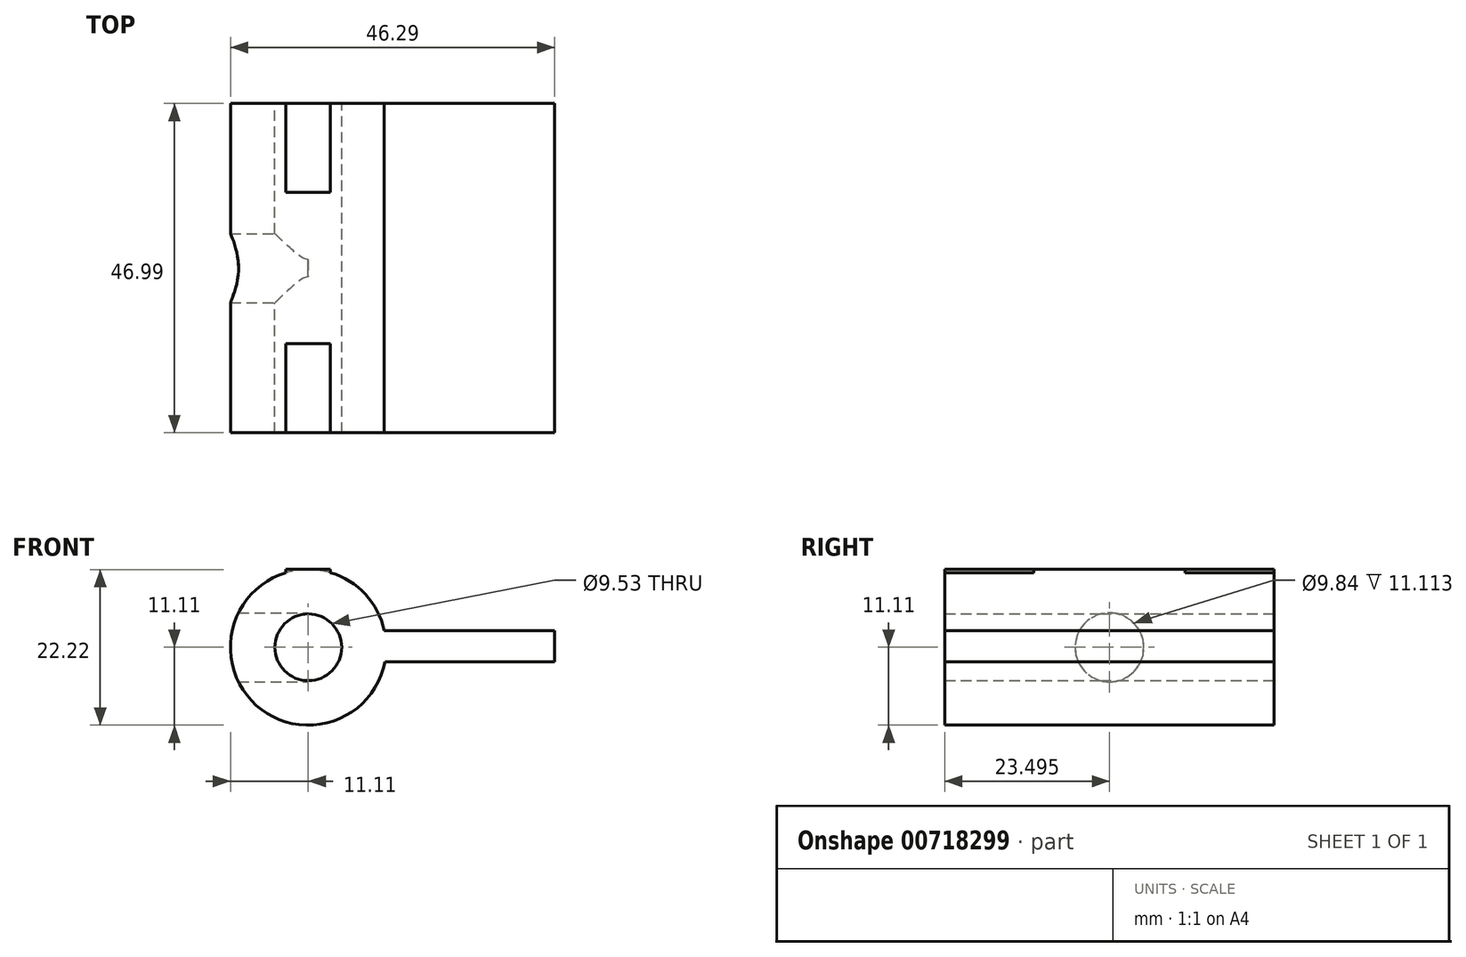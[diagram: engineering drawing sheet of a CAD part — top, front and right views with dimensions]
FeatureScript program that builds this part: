
annotation { "Feature Type Name" : "Feature", "Feature Type Description" : "" }
export const myFeature = defineFeature(function(context is Context, id is Id, definition is map)
    precondition{}
    {
        {
            var Q0;
            Q0=qCreatedBy(makeId("Front.planeOp"),FACE);
            var sketch = newSketch(context, id + "F0", { "sketchPlane" : qUnion([Q0])});
            skCircle(sketch, "E0", {"center": v(0, 0) * mm, "radius": 4.76 * mm});
            skCircle(sketch, "E1", {"center": v(0, 0) * mm, "radius": 11.11 * mm});
            skSolve(sketch);
        }
        {
            var Q0;
            Q0=makeQuery(id+"F0.imprint","IMPRINT",FACE,{"disambiguationData":[TD([[makeQuery(id+"F0.imprint","IMPRINT",EDGE,{"derivedFrom":sQuery(id+"F0.wireOp",EDGE,"E0")}),-1.0]])]});
            extrude(context, id + "F1", {"entities" : qUnion([Q0]), "depth" : 47 * mm, "offsetDistance" : 25.4 * mm});
        }
        {
            var Q0;
            Q0=qCreatedBy(makeId("Right.planeOp"),FACE);
            var sketch = newSketch(context, id + "F2", { "sketchPlane" : qUnion([Q0])});
            skLineSegment(sketch, "E2", {"start": v(-47, 11.11) * mm, "end": v(0, 11.11) * mm});
            skLineSegment(sketch, "E3.bottom", {"start": v(0, 11.11) * mm, "end": v(-12.7, 11.11) * mm});
            skLineSegment(sketch, "E4.bottom", {"start": v(-47, 11.11) * mm, "end": v(-34.3, 11.11) * mm});
            skLineSegment(sketch, "E5", {"start": v(0, -11.11) * mm, "end": v(-47, -11.11) * mm});
            skLineSegment(sketch, "E6.0.0", {"start": v(-47, -11.11) * mm, "end": v(-47, 11.11) * mm});
            skLineSegment(sketch, "E7.top", {"start": v(-47, 7.33) * mm, "end": v(-34.3, 7.33) * mm});
            skLineSegment(sketch, "E7.left", {"start": v(-47, 11.11) * mm, "end": v(-47, 7.33) * mm});
            skLineSegment(sketch, "E7.right", {"start": v(-34.3, 11.11) * mm, "end": v(-34.3, 7.33) * mm});
            skLineSegment(sketch, "E8.bottom", {"start": v(-12.7, 11.11) * mm, "end": v(0, 11.11) * mm});
            skLineSegment(sketch, "E8.top", {"start": v(-12.7, 7.69) * mm, "end": v(0, 7.69) * mm});
            skLineSegment(sketch, "E8.left", {"start": v(-12.7, 11.11) * mm, "end": v(-12.7, 7.69) * mm});
            skLineSegment(sketch, "E8.right", {"start": v(0, 11.11) * mm, "end": v(0, 7.69) * mm});
            skSolve(sketch);
        }
        {
            var Q0;
            {var subQ4=sQuery(id+"F2.wireOp",EDGE,"E7.top");Q0=makeQuery(id+"F2.imprint","IMPRINT",FACE,{"disambiguationData":[TD([[makeQuery(id+"F2.imprint","IMPRINT",EDGE,{"derivedFrom":subQ4}),1.0]])]});}
            var Q1;
            Q1=makeQuery(id+"F2.imprint","IMPRINT",FACE,{"disambiguationData":[TD([[makeQuery(id+"F2.imprint","IMPRINT",EDGE,{"derivedFrom":sQuery(id+"F2.wireOp",EDGE,"E8.top")}),1.0]])]});
            var Q2;
            Q2=makeQuery(id+"F2.imprint","IMPRINT",FACE,{"disambiguationData":[TD([[makeQuery(id+"F2.imprint","IMPRINT",EDGE,{"derivedFrom":sQuery(id+"F2.wireOp",EDGE,"E3.top")}),1.0]])]});
            var Q3;
            Q3=makeQuery(id+"F2.imprint","IMPRINT",FACE,{"disambiguationData":[TD([[makeQuery(id+"F2.imprint","IMPRINT",EDGE,{"derivedFrom":sQuery(id+"F2.wireOp",EDGE,"E4.top")}),-1.0]])]});
            extrude(context, id + "F3", {"entities" : qUnion([Q0, Q1, Q2, Q3]), "operationType" : NewBodyOperationType.ADD, "endBound" : BoundingType.SYMMETRIC, "depth" : 6.35 * mm, "offsetDistance" : 25.4 * mm});
        }
        {
            var Q0;
            Q0=makeQuery(id+"F3.opExtrude","CAP_FACE",FACE,{"disambiguationData":[OSD([sQuery(id+"F2.wireOp",EDGE,"E2"),sQuery(id+"F2.wireOp",EDGE,"E6.0.0"),sQuery(id+"F2.wireOp",EDGE,"E7.top"),sQuery(id+"F2.wireOp",EDGE,"E7.right")])],"isStart":false});
            cPlane(context, id + "F4", {"entities" : qUnion([Q0]), "cplaneType" : CPlaneType.OFFSET, "offset" : 6.6 * mm, "width" : 152.4 * mm, "height" : 152.4 * mm});
        }
        {
            var Q0;
            Q0=qCreatedBy(id+"F4.planeOp",FACE);
            var sketch = newSketch(context, id + "F5", { "sketchPlane" : qUnion([Q0])});
            skLineSegment(sketch, "E9", {"start": v(0, -11.11) * mm, "end": v(-47, -11.11) * mm});
            skLineSegment(sketch, "E10", {"start": v(-34.3, 11.11) * mm, "end": v(-12.7, 11.11) * mm});
            skLineSegment(sketch, "E11.0", {"start": v(-47, 10.65) * mm, "end": v(-47, -11.11) * mm});
            skLineSegment(sketch, "E12.0", {"start": v(0, 10.65) * mm, "end": v(0, -11.11) * mm});
            skLineSegment(sketch, "E13", {"start": v(0, -4.76) * mm, "end": v(-47, -4.76) * mm});
            skLineSegment(sketch, "E14", {"start": v(-47, 4.76) * mm, "end": v(0, 4.76) * mm});
            skLineSegment(sketch, "E15.0", {"start": v(-47, -4.76) * mm, "end": v(-47, 4.76) * mm});
            skLineSegment(sketch, "E16", {"start": v(-47, -0.23) * mm, "end": v(0, 0) * mm, "construction": true});
            skLineSegment(sketch, "E17.bottom", {"start": v(-47, 2.4) * mm, "end": v(0, 2.4) * mm});
            skLineSegment(sketch, "E17.top", {"start": v(-47, -2.04) * mm, "end": v(0, -2.04) * mm});
            skLineSegment(sketch, "E17.left", {"start": v(-47, 2.4) * mm, "end": v(-47, -2.04) * mm});
            skLineSegment(sketch, "E17.right", {"start": v(0, 2.4) * mm, "end": v(0, -2.04) * mm});
            skSolve(sketch);
        }
        {
            var Q0;
            {var subQ0=sQuery(id+"F5.wireOp",EDGE,"E17.bottom");Q0=makeQuery(id+"F5.imprint","IMPRINT",FACE,{"disambiguationData":[TD([[makeQuery(id+"F5.imprint","IMPRINT",EDGE,{"derivedFrom":subQ0}),-1.0]])]});}
            extrude(context, id + "F6", {"entities" : qUnion([Q0]), "operationType" : NewBodyOperationType.ADD, "depth" : 25.4 * mm, "offsetDistance" : 25.4 * mm});
        }
        {
            var Q0;
            Q0=qCreatedBy(makeId("Right.planeOp"),FACE);
            var sketch = newSketch(context, id + "F7", { "sketchPlane" : qUnion([Q0])});
            skCircle(sketch, "E18", {"center": v(-23.5, 0) * mm, "radius": 4.92 * mm});
            skSolve(sketch);
        }
        {
            var Q0;
            Q0 = qSketchRegion(id + "F7", true);
            extrude(context, id + "F8", {"entities" : qUnion([Q0]), "operationType" : NewBodyOperationType.REMOVE, "oppositeDirection" : true, "depth" : 25.4 * mm, "offsetDistance" : 25.4 * mm});
        }
    });
